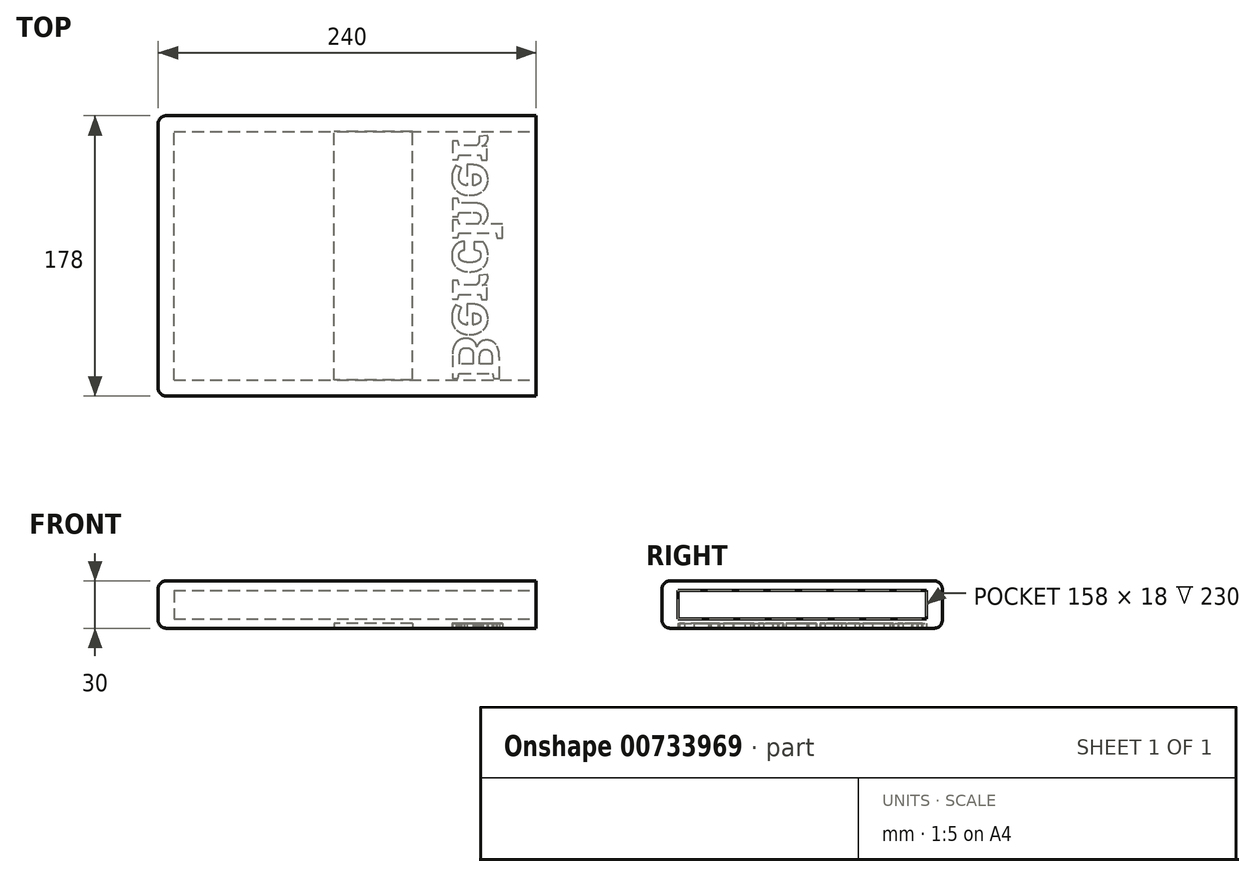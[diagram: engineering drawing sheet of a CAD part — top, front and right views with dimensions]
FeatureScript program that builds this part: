
annotation { "Feature Type Name" : "Feature", "Feature Type Description" : "" }
export const myFeature = defineFeature(function(context is Context, id is Id, definition is map)
    precondition{}
    {
        {
            var Q0;
            Q0=qCreatedBy(makeId("Top.planeOp"),FACE);
            var sketch = newSketch(context, id + "F0", { "sketchPlane" : qUnion([Q0])});
            skLineSegment(sketch, "E0.bottom", {"start": v(-86.6, 94.7) * mm, "end": v(153.4, 94.7) * mm});
            skLineSegment(sketch, "E0.top", {"start": v(-86.6, -83.3) * mm, "end": v(153.4, -83.3) * mm});
            skLineSegment(sketch, "E0.left", {"start": v(-86.6, 94.7) * mm, "end": v(-86.6, -83.3) * mm});
            skLineSegment(sketch, "E0.right", {"start": v(153.4, 94.7) * mm, "end": v(153.4, -83.3) * mm});
            skSolve(sketch);
        }
        {
            var Q0;
            Q0 = qSketchRegion(id + "F0", true);
            extrude(context, id + "F1", {"entities" : qUnion([Q0]), "depth" : 30 * mm, "offsetDistance" : 25 * mm});
        }
        {
            var Q0;
            Q0=makeQuery(id+"F1.opExtrude","SWEPT_FACE",FACE,{"disambiguationData":[OSD([sQuery(id+"F0.wireOp",EDGE,"E0.right")])]});
            var sketch = newSketch(context, id + "F2", { "sketchPlane" : qUnion([Q0])});
            skLineSegment(sketch, "E1.bottom", {"start": v(-73.3, 24) * mm, "end": v(84.7, 24) * mm});
            skLineSegment(sketch, "E1.top", {"start": v(-73.3, 6) * mm, "end": v(84.7, 6) * mm});
            skLineSegment(sketch, "E1.left", {"start": v(-73.3, 24) * mm, "end": v(-73.3, 6) * mm});
            skLineSegment(sketch, "E1.right", {"start": v(84.7, 24) * mm, "end": v(84.7, 6) * mm});
            skSolve(sketch);
        }
        {
            var Q0;
            Q0 = qSketchRegion(id + "F2", true);
            extrude(context, id + "F3", {"entities" : qUnion([Q0]), "operationType" : NewBodyOperationType.REMOVE, "oppositeDirection" : true, "depth" : 230 * mm, "offsetDistance" : 25 * mm});
        }
        {
            var Q0;
            Q0=makeQuery(id+"F1.opExtrude","CAP_EDGE",EDGE,{"disambiguationData":[OSD([sQuery(id+"F0.wireOp",EDGE,"E0.left")])],"isStart":false});
            var Q1;
            Q1=makeQuery(id+"F1.opExtrude","CAP_EDGE",EDGE,{"disambiguationData":[OSD([sQuery(id+"F0.wireOp",EDGE,"E0.top")])],"isStart":false});
            var Q2;
            Q2=makeQuery(id+"F1.opExtrude","CAP_EDGE",EDGE,{"disambiguationData":[OSD([sQuery(id+"F0.wireOp",EDGE,"E0.bottom")])],"isStart":false});
            var Q3;
            Q3=makeQuery(id+"F1.opExtrude","CAP_EDGE",EDGE,{"disambiguationData":[OSD([sQuery(id+"F0.wireOp",EDGE,"E0.left")])],"isStart":true});
            var Q4;
            Q4=makeQuery(id+"F1.opExtrude","CAP_EDGE",EDGE,{"disambiguationData":[OSD([sQuery(id+"F0.wireOp",EDGE,"E0.bottom")])],"isStart":true});
            var Q5;
            Q5=makeQuery(id+"F1.opExtrude","CAP_EDGE",EDGE,{"disambiguationData":[OSD([sQuery(id+"F0.wireOp",EDGE,"E0.top")])],"isStart":true});
            var Q6;
            Q6=makeQuery(id+"F1.opExtrude","SWEPT_EDGE",EDGE,{"disambiguationData":[OSD([sQuery(id+"F0.wireOp",EDGE,"E0.bottom"),sQuery(id+"F0.wireOp",EDGE,"E0.left")])]});
            var Q7;
            Q7=makeQuery(id+"F1.opExtrude","SWEPT_EDGE",EDGE,{"disambiguationData":[OSD([sQuery(id+"F0.wireOp",EDGE,"E0.top"),sQuery(id+"F0.wireOp",EDGE,"E0.left")])]});
            fillet(context, id + "F4", {"entities" : qUnion([Q0, Q1, Q2, Q3, Q4, Q5, Q6, Q7]), "radius" : 5 * mm, "tangentPropagation" : true, "allowEdgeOverflow" : false});
        }
        {
            var Q0;
            Q0=makeQuery(id+"F1.opExtrude","CAP_FACE",FACE,{"disambiguationData":[OSD([sQuery(id+"F0.wireOp",EDGE,"E0.bottom"),sQuery(id+"F0.wireOp",EDGE,"E0.top"),sQuery(id+"F0.wireOp",EDGE,"E0.left"),sQuery(id+"F0.wireOp",EDGE,"E0.right")])],"isStart":true});
            var sketch = newSketch(context, id + "F5", { "sketchPlane" : qUnion([Q0])});
            skText(sketch, "E2", { "text": "Bercher", "fontName": "RobotoSlab-Bold.ttf"});
            const initialGuessF5  = {"E2": [0.10031, 0.0733, 0, -1, 0.0301]};
            skSetInitialGuess(sketch, initialGuessF5);
            skSolve(sketch);
        }
        {
            var Q0;
            Q0 = qSketchRegion(id + "F5", true);
            extrude(context, id + "F6", {"entities" : qUnion([Q0]), "operationType" : NewBodyOperationType.REMOVE, "oppositeDirection" : true, "depth" : 3 * mm, "offsetDistance" : 25 * mm});
        }
        {
            var Q0;
            {var subQ0=sQuery(id+"F0.wireOp",EDGE,"E0.bottom");var subQ1=sQuery(id+"F0.wireOp",EDGE,"E0.left");var subQ2=sQuery(id+"F0.wireOp",EDGE,"E0.top");var subQ3=sQuery(id+"F0.wireOp",EDGE,"E0.right");Q0=makeQuery(id+"F6.boolean.opBoolean","SPLIT",FACE,{"disambiguationData":[TD([makeQuery(id+"F1.opExtrude","SWEPT_FACE",FACE,{"disambiguationData":[OSD([subQ3])]})])],"derivedFrom":makeQuery(id+"F1.opExtrude","CAP_FACE",FACE,{"disambiguationData":[OSD([subQ0,subQ2,subQ1,subQ3])],"isStart":true})});}
            var sketch = newSketch(context, id + "F7", { "sketchPlane" : qUnion([Q0])});
            skLineSegment(sketch, "E3.bottom", {"start": v(74.95, 73.3) * mm, "end": v(24.95, 73.3) * mm});
            skLineSegment(sketch, "E3.top", {"start": v(74.95, -84.7) * mm, "end": v(24.95, -84.7) * mm});
            skLineSegment(sketch, "E3.left", {"start": v(74.95, 73.3) * mm, "end": v(74.95, -84.7) * mm});
            skLineSegment(sketch, "E3.right", {"start": v(24.95, 73.3) * mm, "end": v(24.95, -84.7) * mm});
            skSolve(sketch);
        }
        {
            var Q0;
            Q0=makeQuery(id+"F7.imprint","IMPRINT",FACE,{"disambiguationData":[TD([[makeQuery(id+"F7.imprint","IMPRINT",EDGE,{"derivedFrom":sQuery(id+"F7.wireOp",EDGE,"E3.bottom")}),1.0]])]});
            extrude(context, id + "F8", {"entities" : qUnion([Q0]), "operationType" : NewBodyOperationType.REMOVE, "oppositeDirection" : true, "depth" : 3 * mm, "offsetDistance" : 25 * mm});
        }
    });
